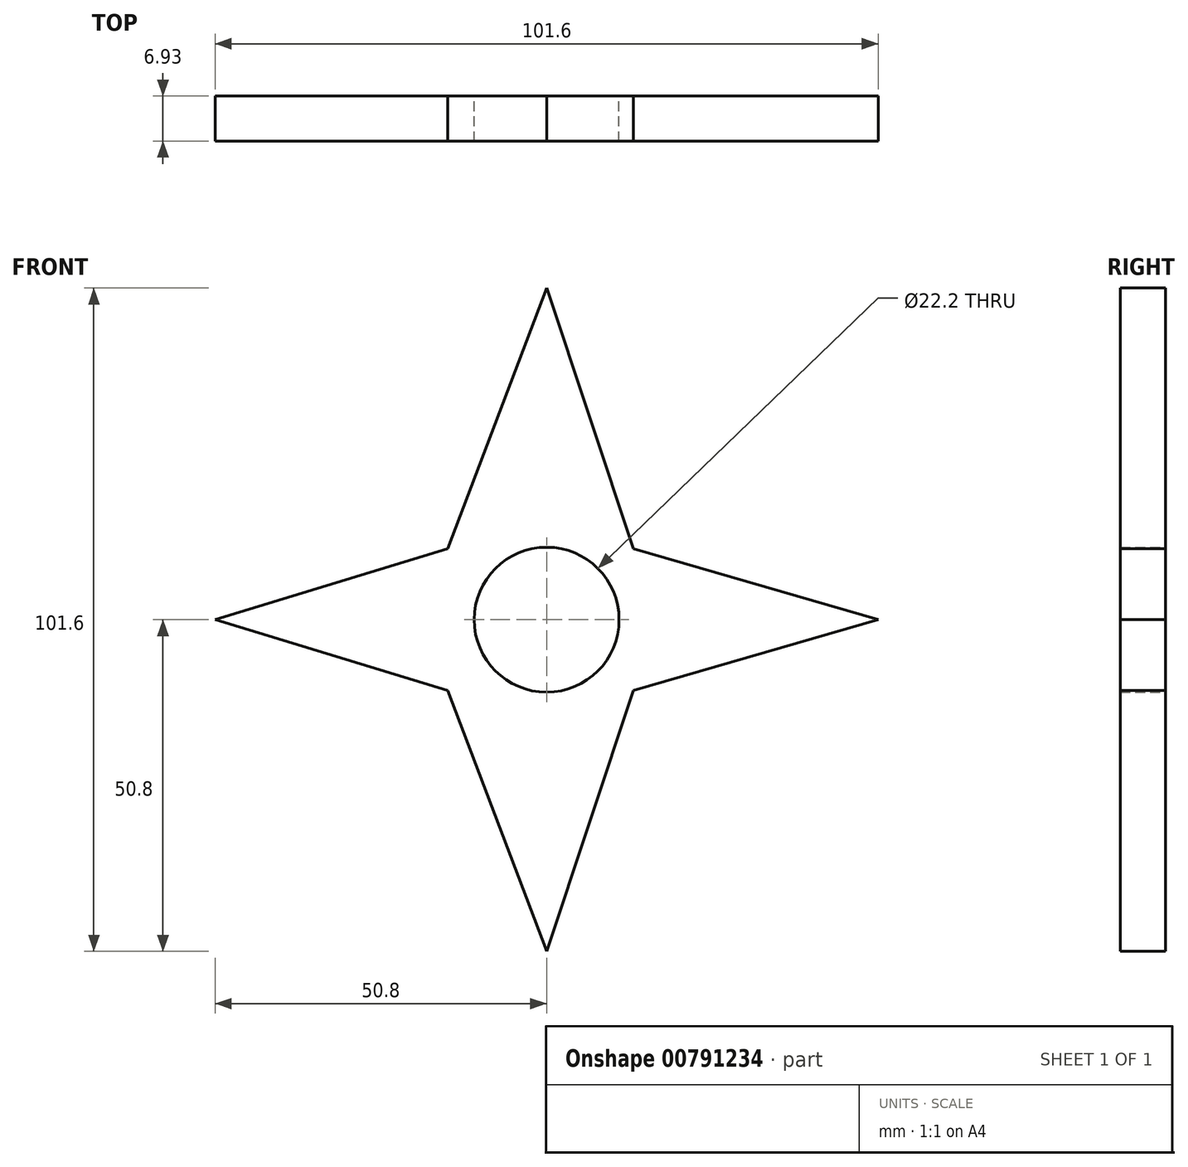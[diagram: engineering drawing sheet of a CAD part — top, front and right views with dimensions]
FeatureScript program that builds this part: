
annotation { "Feature Type Name" : "Feature", "Feature Type Description" : "" }
export const myFeature = defineFeature(function(context is Context, id is Id, definition is map)
    precondition{}
    {
        {
            var Q0;
            Q0=qCreatedBy(makeId("Front.planeOp"),FACE);
            var sketch = newSketch(context, id + "F0", { "sketchPlane" : qUnion([Q0])});
            skCircle(sketch, "E0", {"center": v(0, 0) * mm, "radius": 4 * mm});
            skCircle(sketch, "E1", {"center": v(0, 0) * mm, "radius": 11.1 * mm});
            skLineSegment(sketch, "E2", {"start": v(-15.13, 10.9) * mm, "end": v(0, 50.8) * mm});
            skLineSegment(sketch, "E3", {"start": v(-15.13, 10.9) * mm, "end": v(-50.8, 0) * mm});
            skLineSegment(sketch, "E4", {"start": v(-50.8, 0) * mm, "end": v(-15.13, -10.84) * mm});
            skLineSegment(sketch, "E5", {"start": v(-15.13, -10.84) * mm, "end": v(0, -50.8) * mm});
            skLineSegment(sketch, "E6", {"start": v(0, -50.8) * mm, "end": v(13.28, -10.84) * mm});
            skLineSegment(sketch, "E7", {"start": v(0, 50.8) * mm, "end": v(13.28, 10.9) * mm});
            skLineSegment(sketch, "E8", {"start": v(13.28, 10.9) * mm, "end": v(50.8, 0) * mm});
            skLineSegment(sketch, "E9", {"start": v(50.8, 0) * mm, "end": v(13.28, -10.84) * mm});
            skSolve(sketch);
        }
        {
            var Q0;
            Q0=makeQuery(id+"F0.imprint","IMPRINT",FACE,{"disambiguationData":[TD([[makeQuery(id+"F0.imprint","IMPRINT",EDGE,{"derivedFrom":sQuery(id+"F0.wireOp",EDGE,"E1")}),-1.0]])]});
            extrude(context, id + "F1", {"entities" : qUnion([Q0]), "depth" : 6.93 * mm, "offsetDistance" : 25.4 * mm});
        }
    });
